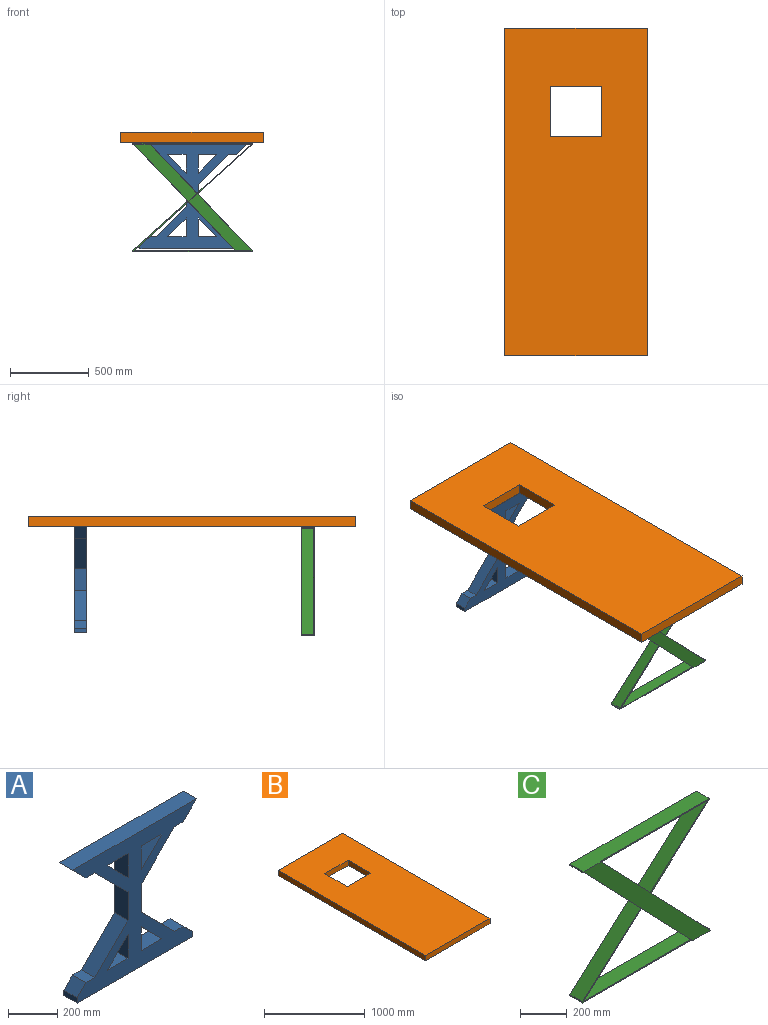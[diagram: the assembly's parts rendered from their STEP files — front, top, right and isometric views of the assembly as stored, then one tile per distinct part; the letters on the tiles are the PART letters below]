
ASSEMBLY  parts=3 mates=2
PART A: 32 faces, bbox 711.2x76.2x673.1 mm
  f0: plane 118.66x118.66mm, normal (0.71,0,-0.71), area 12786.9mm2, adj f1,f29,f30,f31
  f1: plane 118.66x76.2mm, normal (-1,0,0), area 9041.7mm2, adj f0,f29,f30,f31
  f2: plane 118.66x76.2mm, normal (1,0,0), area 9041.7mm2, adj f3,f25,f30,f31
  f3: plane 118.66x118.66mm, normal (-0.71,0,-0.71), area 12786.9mm2, adj f2,f25,f30,f31
  f4: plane 118.66x118.66mm, normal (-0.71,0,0.71), area 12786.9mm2, adj f5,f26,f30,f31
  f5: plane 118.66x76.2mm, normal (1,0,0), area 9041.7mm2, adj f4,f26,f30,f31
  f6: plane 190.5x190.5mm, normal (-0.71,0,-0.71), area 20528.9mm2, adj f7,f27,f30,f31
  f7: plane 139.7x76.2mm, normal (-1,0,0), area 10645.1mm2, adj f6,f8,f30,f31
  f8: plane 190.5x190.5mm, normal (-0.71,0,0.71), area 20528.9mm2, adj f7,f9,f30,f31
  f9: plane 76.2x50.8mm, normal (0,0,1), area 3871mm2, adj f8,f10,f30,f31
  f10: plane 76.2x50.8mm, normal (-0.71,0,0.71), area 5474.4mm2, adj f9,f11,f30,f31
  f11: plane 76.2x25.4mm, normal (-1,0,0), area 1935.5mm2, adj f10,f12,f30,f31
  f12: plane 660.4x76.2mm, normal (0,0,-1), area 50322.5mm2, adj f11,f13,f30,f31
  f13: plane 76.2x25.4mm, normal (1,0,0), area 1935.5mm2, adj f12,f14,f30,f31
  f14: plane 76.2x50.8mm, normal (0.71,0,0.71), area 5474.4mm2, adj f13,f15,f30,f31
  f15: plane 76.2x50.8mm, normal (0,0,1), area 3871mm2, adj f14,f16,f30,f31
  f16: plane 190.5x190.5mm, normal (0.71,0,0.71), area 20528.9mm2, adj f15,f17,f30,f31
  f17: plane 139.7x76.2mm, normal (1,0,0), area 10645.1mm2, adj f16,f18,f30,f31
  f18: plane 190.5x190.5mm, normal (0.71,0,-0.71), area 20528.9mm2, adj f17,f19,f30,f31
  f19: plane 76.2x50.8mm, normal (0,0,-1), area 3871mm2, adj f18,f20,f30,f31
  f20: plane 76.2x76.2mm, normal (0.71,0,-0.71), area 8211.5mm2, adj f19,f21,f30,f31
  f21: plane 711.2x76.2mm, normal (0,0,1), area 54193.4mm2, adj f20,f22,f30,f31
  f22: plane 76.2x76.2mm, normal (-0.71,0,-0.71), area 8211.5mm2, adj f21,f27,f30,f31
  f23: plane 118.66x76.2mm, normal (-1,0,0), area 9041.7mm2, adj f24,f28,f30,f31
  f24: plane 118.66x118.66mm, normal (0.71,0,0.71), area 12786.9mm2, adj f23,f28,f30,f31
  f25: plane 118.66x76.2mm, normal (0,0,1), area 9041.7mm2, adj f2,f3,f30,f31
  f26: plane 118.66x76.2mm, normal (0,0,-1), area 9041.7mm2, adj f4,f5,f30,f31
  f27: plane 76.2x50.8mm, normal (0,0,-1), area 3871mm2, adj f6,f22,f30,f31
  f28: plane 118.66x76.2mm, normal (0,0,-1), area 9041.7mm2, adj f23,f24,f30,f31
  f29: plane 118.66x76.2mm, normal (0,0,1), area 9041.7mm2, adj f0,f1,f30,f31
  f30: plane 711.2x673.1mm, normal (0,-1,0), area 180227.3mm2, adj f0,f1,f2,f3,f4,f5,f6,f7
  f31: plane 711.2x673.1mm, normal (0,1,0), area 180227.3mm2, adj f0,f1,f2,f3,f4,f5,f6,f7
PART B: 10 faces, bbox 901.7x2070.1x63.5 mm
  f0: plane 314.33x63.5mm, normal (1,0,0), area 19959.6mm2, adj f1,f7,f8,f9
  f1: plane 327.03x63.5mm, normal (0,-1,0), area 20766.1mm2, adj f0,f2,f8,f9
  f2: plane 314.33x63.5mm, normal (-1,0,0), area 19959.6mm2, adj f1,f7,f8,f9
  f3: plane 2070.1x63.5mm, normal (1,0,0), area 131451.3mm2, adj f4,f6,f8,f9
  f4: plane 901.7x63.5mm, normal (0,1,0), area 57257.9mm2, adj f3,f5,f8,f9
  f5: plane 2070.1x63.5mm, normal (-1,0,0), area 131451.3mm2, adj f4,f6,f8,f9
  f6: plane 901.7x63.5mm, normal (0,-1,0), area 57257.9mm2, adj f3,f5,f8,f9
  f7: plane 327.03x63.5mm, normal (0,1,0), area 20766.1mm2, adj f0,f2,f8,f9
  f8: plane 2070.1x901.7mm, normal (0,0,1), area 1763817mm2, adj f0,f1,f2,f3,f4,f5,f6,f7
  f9: plane 2070.1x901.7mm, normal (0,0,-1), area 1763817mm2, adj f0,f1,f2,f3,f4,f5,f6,f7
PART C: 20 faces, bbox 762x82.6x685.8 mm
  f0: plane 656.51x319.78mm, normal (0,-1,0), area 7112.9mm2, adj f4,f5,f6,f8,f9,f17
  f1: plane 6.35x6.08mm, normal (0,-1,0), area 19.3mm2, adj f7,f8,f16
  f2: plane 6.35x6.08mm, normal (0,-1,0), area 19.3mm2, adj f3,f12,f17
  f3: plane 752.48x76.2mm, normal (0,0,-1), area 57338.6mm2, adj f2,f4,f12,f13,f14,f15
  f4: plane 752.48x673.1mm, normal (-0.67,0,0.75), area 76931.2mm2, adj f0,f3,f5,f13,f14,f15
  f5: plane 76.2x6.35mm, normal (-1,0,0), area 483.9mm2, adj f0,f4,f6,f14
  f6: plane 762x82.55mm, normal (0,0,-1), area 58734.2mm2, adj f0,f5,f7,f14,f16,f17,f18
  f7: plane 76.2x6.35mm, normal (1,0,0), area 483.9mm2, adj f1,f6,f8,f14
  f8: plane 752.48x76.2mm, normal (0,0,1), area 57338.6mm2, adj f0,f1,f7,f9,f14,f19
  f9: plane 752.48x673.1mm, normal (0.67,0,-0.75), area 76931.2mm2, adj f0,f8,f10,f13,f14,f19
  f10: plane 76.2x6.35mm, normal (1,0,0), area 483.9mm2, adj f9,f11,f13,f14
  f11: plane 762x82.55mm, normal (0,0,1), area 58734.2mm2, adj f10,f12,f13,f14,f16,f17,f18
  f12: plane 76.2x6.35mm, normal (-1,0,0), area 483.9mm2, adj f2,f3,f11,f14
  f13: plane 656.51x319.78mm, normal (0,-1,0), area 7112.9mm2, adj f3,f4,f9,f10,f11,f16
  f14: plane 762x685.8mm, normal (0,1,0), area 16088.3mm2, adj f3,f4,f5,f6,f7,f8,f9,f10
  f15: plane 401.14x359.67mm, normal (0,1,0), area 35259.6mm2, adj f3,f4,f16,f17
  f16: plane 685.8x656.51mm, normal (0.72,0,0.69), area 6028.6mm2, adj f1,f6,f11,f13,f15,f18,f19
  f17: plane 685.8x656.51mm, normal (-0.72,0,-0.69), area 6028.6mm2, adj f0,f2,f6,f11,f15,f18,f19
  f18: plane 762x685.8mm, normal (0,-1,0), area 72343.1mm2, adj f6,f11,f16,f17
  f19: plane 401.14x359.67mm, normal (0,1,0), area 35259.6mm2, adj f8,f9,f16,f17
PLACE A t=(-251.68,773.62,-115)mm
PLACE B t=(-252.72,31.2,-115)mm
PLACE C t=(-247.62,-661.36,-806.34)mm
MATE parallel B.f9 <-> C.f11  axis (0,0,-1) through (-252.72,1.5,-115)mm
MATE planar A.f21 <-> B.f9  axis (0,0,1) through (-251.68,735.52,-115)mm
